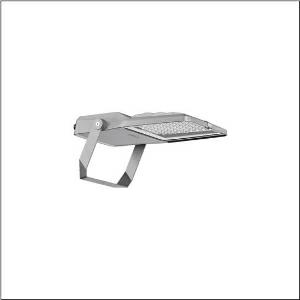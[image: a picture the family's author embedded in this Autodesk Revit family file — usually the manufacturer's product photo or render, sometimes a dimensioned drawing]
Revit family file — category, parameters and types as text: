
# Revit family: floodlight_fl_21_mini___pl52_5xa7776d2d1a_6cb1
name_source: partatom
category: Lighting Fixtures
units: mm (PartAtom-declared; Revit-internal decimal feet)

## family parameters
Cut with Voids When Loaded = No
Host = Face
Light Source = No
Part Type = Normal
Room Calculation Point = No
Round Connector Dimension = Use Diameter
Shared = No

## types (1)
- --- (1 x LED, 17840 lm, 142.9 W, 3000K)
    Apparent Load = 143 VA
    CIE Flux Codes = 26 60 98 100 100
    Color Rendering = 70
    Color Temperature = 3000K
    Default Elevation = 1800 mm
    Description = Floodlight FL 21 mini, floodlight, primary light control with lens, of PMMA, primary optical cover: protective disc, of toughened safety glass, transparent, light distribution: PL52, light emission: direct distribution, installation type: surface-mounted, LED, High Power LED, rated luminous flux: 17.840lm, luminous efficacy: 125lm/W, light colour: 730, colour temperature: 3000K, control gear: Smart Interface (Zhaga), control: flexible luminous flux parameterisation, time-dependent luminous flux control, constant luminous flux control, overheat protection, pre-setting: logarithmic dimming characteristic, with terminal, 6-pole, mains connection: 220..240V, AC, 50/60Hz, start of lifetime: 143W, end of service life: 151W, reduction: 63W, luminaire housing, of diecast aluminium, powder-coated, Siteco® metallic grey (DB 702S), corrosivity category C5 mid according to DIN EN ISO 12944, suitable for swimming pools, chlorine-resistant, sealing non-destructively replaceable, mounting bracket, of steel, galvanised, powder-coated, Siteco® metallic grey (DB 702S), Smart Interface below and above, protection rating (complete): IP66, insulation class (complete): insulation class II (safety insulation), certification: CE, ENEC, VDE, protection symbol: D, impact resistance: IK08, permissible operating ambient temperature: -40..+40°C, permissible operating ambient temperature for outdoor applications: -40..+50°C, standard: DIN EN 12944, LABS conformity tested according to VDMA 24364:2018-05, packaging unit: 1 piece

Light Distribution: PL52
    Height = 70 mm
    Lamp = 1 x LED
    Lamp Light Flux = 17840 lm
    Lamp Power = 142.9 W
    Lamp count = 1
    Length = 485 mm
    Luminous efficacy = 125 lm/W
    Manufacturer = Siteco
    ModVariant = No
    Model = 5XA7776D2D1A
    Number of Poles = 1
    OnlyDefault = Yes
    Power Factor = 1
    Product Name = Floodlight FL 21 mini | PL52
    Product group = floodlight | pylon annexe
    ProductGroupID = 6200
    Protection Class = Protection class II
    Protection Degree = IP 66
    RLX_Detail_Level = 1
    RLX_Emergency_Light_Flux = 0 lm
    RLX_Emergency_Type = 0
    RLX_Emergency_Type_DB = No
    RlxData = <blob elided: 96629 chars, md5=c3408de4>
    Socket = socket
    Standby Power = 0 W
    System Light Flux = 17840 lm
    System Power = 143 W
    Type Comments = factory setting: luminous flux: 100 % | dim-lin: 254 | 730 mA
    Type Image = l_1006845.jpg
    URL = http://relux.com
    VarID = @adj_163150
    Voltage = 0 V
    Weight = 0.00 kg
    Width = 337 mm

## geometry (parser evidence)
native form markers: Blend x4, Sweep x10
no freeform markers — native parametric forms only
